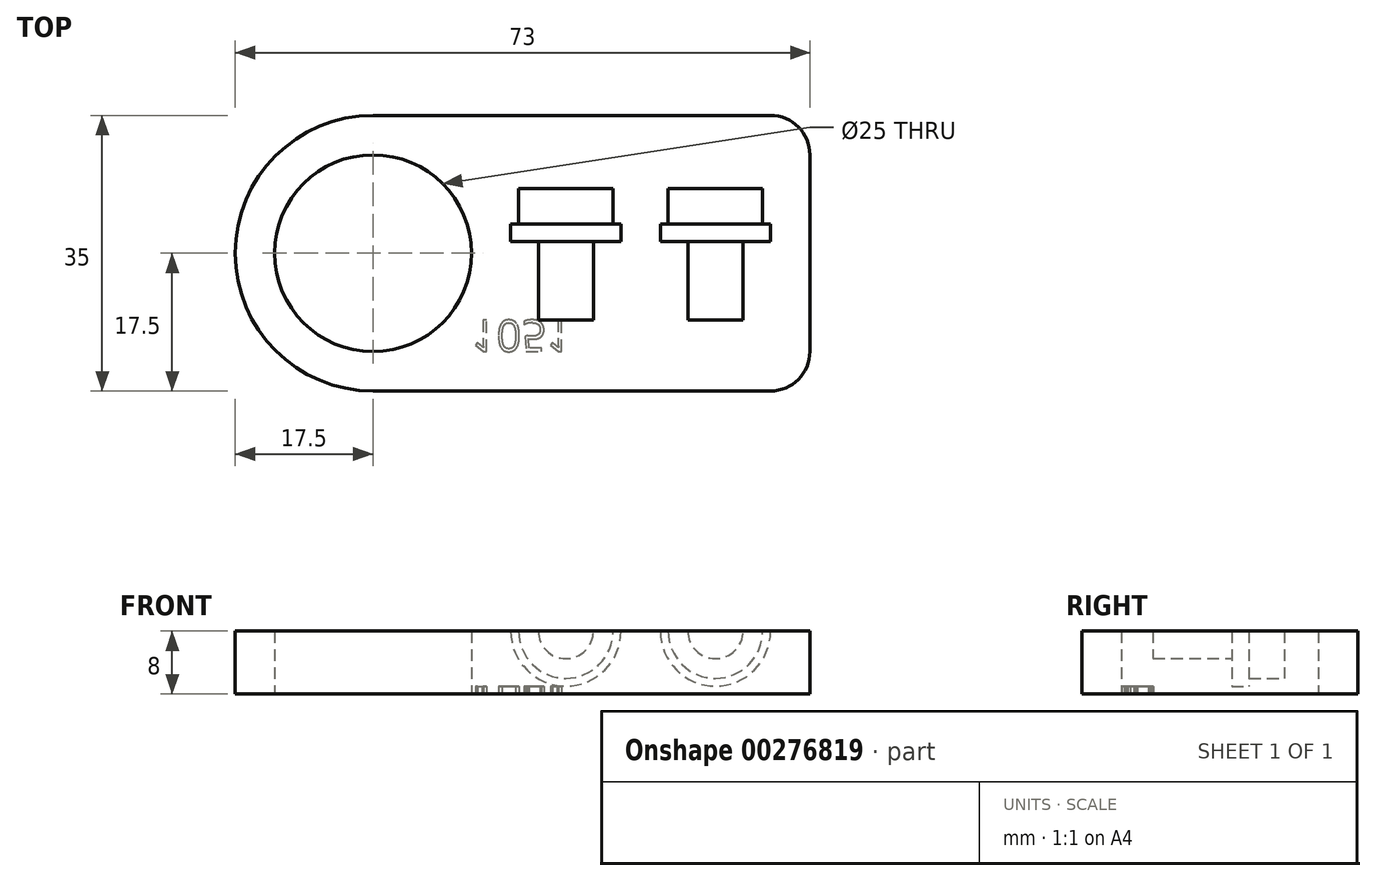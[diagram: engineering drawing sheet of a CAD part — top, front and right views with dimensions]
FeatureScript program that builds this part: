
annotation { "Feature Type Name" : "Feature", "Feature Type Description" : "" }
export const myFeature = defineFeature(function(context is Context, id is Id, definition is map)
    precondition{}
    {
        {
            var Q0;
            Q0=qCreatedBy(makeId("Top.planeOp"),FACE);
            var sketch = newSketch(context, id + "F0", { "sketchPlane" : qUnion([Q0])});
            skLineSegment(sketch, "E0.bottom", {"start": v(17.5, 0) * mm, "end": v(68, 0) * mm});
            skLineSegment(sketch, "E0.top", {"start": v(17.5, 35) * mm, "end": v(68, 35) * mm});
            skLineSegment(sketch, "E0.left", {"start": v(0, 17.5) * mm, "end": v(0, 17.5) * mm});
            skLineSegment(sketch, "E0.right", {"start": v(73, 5) * mm, "end": v(73, 30) * mm});
            skLineSegment(sketch, "E1.bottom", {"start": v(0, 0) * mm, "end": v(17.5, 0) * mm, "construction": true});
            skLineSegment(sketch, "E1.top", {"start": v(0, 17.5) * mm, "end": v(17.5, 17.5) * mm, "construction": true});
            skLineSegment(sketch, "E1.left", {"start": v(0, 0) * mm, "end": v(0, 17.5) * mm, "construction": true});
            skLineSegment(sketch, "E1.right", {"start": v(17.5, 0) * mm, "end": v(17.5, 17.5) * mm, "construction": true});
            skCircle(sketch, "E2", {"center": v(17.5, 17.5) * mm, "radius": 12.5 * mm});
            skPoint(sketch, "E3.visualSharp", {"position": v(0, 0) * mm});
            skArc(sketch, "E3.filletArc", {"start": v(0, 17.5) * mm, "mid": v(5.13, 5.13) * mm, "end": v(17.5, 0) * mm});
            skPoint(sketch, "E4.visualSharp", {"position": v(0, 35) * mm});
            skArc(sketch, "E4.filletArc", {"start": v(17.5, 35) * mm, "mid": v(5.13, 29.87) * mm, "end": v(0, 17.5) * mm});
            skPoint(sketch, "E5.visualSharp", {"position": v(73, 35) * mm});
            skArc(sketch, "E5.filletArc", {"start": v(73, 30) * mm, "mid": v(71.54, 33.54) * mm, "end": v(68, 35) * mm});
            skPoint(sketch, "E6.visualSharp", {"position": v(73, 0) * mm});
            skArc(sketch, "E6.filletArc", {"start": v(68, 0) * mm, "mid": v(71.54, 1.46) * mm, "end": v(73, 5) * mm});
            skSolve(sketch);
        }
        {
            var Q0;
            Q0=makeQuery(id+"F0.imprint","IMPRINT",FACE,{"disambiguationData":[TD([[makeQuery(id+"F0.imprint","IMPRINT",EDGE,{"derivedFrom":sQuery(id+"F0.wireOp",EDGE,"E0.bottom")}),1.0]])]});
            extrude(context, id + "F1", {"entities" : qUnion([Q0]), "depth" : 8 * mm});
        }
        {
            var Q0;
            Q0=makeQuery(id+"F1.opExtrude","CAP_FACE",FACE,{"disambiguationData":[OSD([sQuery(id+"F0.wireOp",EDGE,"E0.bottom"),sQuery(id+"F0.wireOp",EDGE,"E0.top"),sQuery(id+"F0.wireOp",EDGE,"E0.right"),sQuery(id+"F0.wireOp",EDGE,"E2"),sQuery(id+"F0.wireOp",EDGE,"E3.filletArc"),sQuery(id+"F0.wireOp",EDGE,"E4.filletArc"),sQuery(id+"F0.wireOp",EDGE,"E5.filletArc"),sQuery(id+"F0.wireOp",EDGE,"E6.filletArc")])],"isStart":false});
            var sketch = newSketch(context, id + "F2", { "sketchPlane" : qUnion([Q0])});
            skLineSegment(sketch, "E7.bottom", {"start": v(0, 0) * mm, "end": v(42, 0) * mm, "construction": true});
            skLineSegment(sketch, "E7.top", {"start": v(0, 9) * mm, "end": v(42, 9) * mm, "construction": true});
            skLineSegment(sketch, "E7.left", {"start": v(0, 0) * mm, "end": v(0, 9) * mm, "construction": true});
            skLineSegment(sketch, "E7.right", {"start": v(42, 0) * mm, "end": v(42, 9) * mm, "construction": true});
            skLineSegment(sketch, "E8.bottom", {"start": v(42, 9) * mm, "end": v(45.5, 9) * mm});
            skLineSegment(sketch, "E8.left", {"start": v(42, 9) * mm, "end": v(42, 19) * mm});
            skLineSegment(sketch, "E8.right", {"start": v(45.5, 9) * mm, "end": v(45.5, 19) * mm});
            skLineSegment(sketch, "E9.bottom", {"start": v(45.5, 19) * mm, "end": v(49, 19) * mm});
            skLineSegment(sketch, "E9.top", {"start": v(48, 21.2) * mm, "end": v(49, 21.2) * mm});
            skLineSegment(sketch, "E9.left", {"start": v(42, 19) * mm, "end": v(42, 21.2) * mm});
            skLineSegment(sketch, "E9.right", {"start": v(49, 19) * mm, "end": v(49, 21.2) * mm});
            skLineSegment(sketch, "E10.top", {"start": v(42, 25.7) * mm, "end": v(48, 25.7) * mm});
            skLineSegment(sketch, "E10.left", {"start": v(42, 21.2) * mm, "end": v(42, 25.7) * mm});
            skLineSegment(sketch, "E10.right", {"start": v(48, 21.2) * mm, "end": v(48, 25.7) * mm});
            skLineSegment(sketch, "E11", {"start": v(42, 9) * mm, "end": v(61, 9) * mm, "construction": true});
            skLineSegment(sketch, "E12.bottom", {"start": v(61, 9) * mm, "end": v(64.5, 9) * mm});
            skLineSegment(sketch, "E12.left", {"start": v(61, 9) * mm, "end": v(61, 19) * mm});
            skLineSegment(sketch, "E12.right", {"start": v(64.5, 9) * mm, "end": v(64.5, 19) * mm});
            skLineSegment(sketch, "E13.bottom", {"start": v(64.5, 19) * mm, "end": v(68, 19) * mm});
            skLineSegment(sketch, "E13.top", {"start": v(67, 21.2) * mm, "end": v(68, 21.2) * mm});
            skLineSegment(sketch, "E13.left", {"start": v(61, 19) * mm, "end": v(61, 21.2) * mm});
            skLineSegment(sketch, "E13.right", {"start": v(68, 19) * mm, "end": v(68, 21.2) * mm});
            skLineSegment(sketch, "E14.top", {"start": v(61, 25.7) * mm, "end": v(67, 25.7) * mm});
            skLineSegment(sketch, "E14.left", {"start": v(61, 21.2) * mm, "end": v(61, 25.7) * mm});
            skLineSegment(sketch, "E14.right", {"start": v(67, 21.2) * mm, "end": v(67, 25.7) * mm});
            skSolve(sketch);
        }
        {
            var Q0;
            Q0=makeQuery(id+"F2.imprint","IMPRINT",FACE,{"disambiguationData":[TD([[makeQuery(id+"F2.imprint","IMPRINT",EDGE,{"derivedFrom":sQuery(id+"F2.wireOp",EDGE,"E8.bottom")}),1.0]])]});
            var Q1;
            Q1=sQuery(id+"F2.wireOp",EDGE,"E8.left");
            revolve(context, id + "F3", {"operationType" : NewBodyOperationType.REMOVE, "entities" : qUnion([Q0]), "axis" : qUnion([Q1]), "revolveType" : RevolveType.FULL, "oppositeDirection" : true});
        }
        {
            var Q0;
            Q0=makeQuery(id+"F2.imprint","IMPRINT",FACE,{"disambiguationData":[TD([[makeQuery(id+"F2.imprint","IMPRINT",EDGE,{"derivedFrom":sQuery(id+"F2.wireOp",EDGE,"E12.bottom")}),1.0]])]});
            var Q1;
            Q1=sQuery(id+"F2.wireOp",EDGE,"E12.left");
            revolve(context, id + "F4", {"operationType" : NewBodyOperationType.REMOVE, "entities" : qUnion([Q0]), "axis" : qUnion([Q1]), "revolveType" : RevolveType.FULL, "oppositeDirection" : true});
        }
        {
            var Q0;
            Q0=makeQuery(id+"F1.opExtrude","CAP_FACE",FACE,{"disambiguationData":[OSD([sQuery(id+"F0.wireOp",EDGE,"E0.bottom"),sQuery(id+"F0.wireOp",EDGE,"E0.top"),sQuery(id+"F0.wireOp",EDGE,"E0.right"),sQuery(id+"F0.wireOp",EDGE,"E2"),sQuery(id+"F0.wireOp",EDGE,"E3.filletArc"),sQuery(id+"F0.wireOp",EDGE,"E4.filletArc"),sQuery(id+"F0.wireOp",EDGE,"E5.filletArc"),sQuery(id+"F0.wireOp",EDGE,"E6.filletArc")])],"isStart":true});
            var sketch = newSketch(context, id + "F5", { "sketchPlane" : qUnion([Q0])});
            skLineSegment(sketch, "E15.bottom", {"start": v(0, 0) * mm, "end": v(30, 0) * mm, "construction": true});
            skLineSegment(sketch, "E15.top", {"start": v(0, -5) * mm, "end": v(30, -5) * mm, "construction": true});
            skLineSegment(sketch, "E15.left", {"start": v(0, 0) * mm, "end": v(0, -5) * mm, "construction": true});
            skLineSegment(sketch, "E15.right", {"start": v(30, 0) * mm, "end": v(30, -5) * mm, "construction": true});
            skText(sketch, "E16", { "text": "1051", "fontName": "OpenSans-Regular.ttf"});
            const initialGuessF5  = {"E16": [0.03, -0.009, 1, 0, 0.004]};
            skSetInitialGuess(sketch, initialGuessF5);
            skSolve(sketch);
        }
        {
            var Q0;
            Q0 = qSketchRegion(id + "F5", true);
            extrude(context, id + "F6", {"entities" : qUnion([Q0]), "operationType" : NewBodyOperationType.REMOVE, "oppositeDirection" : true, "depth" : 1 * mm});
        }
    });
